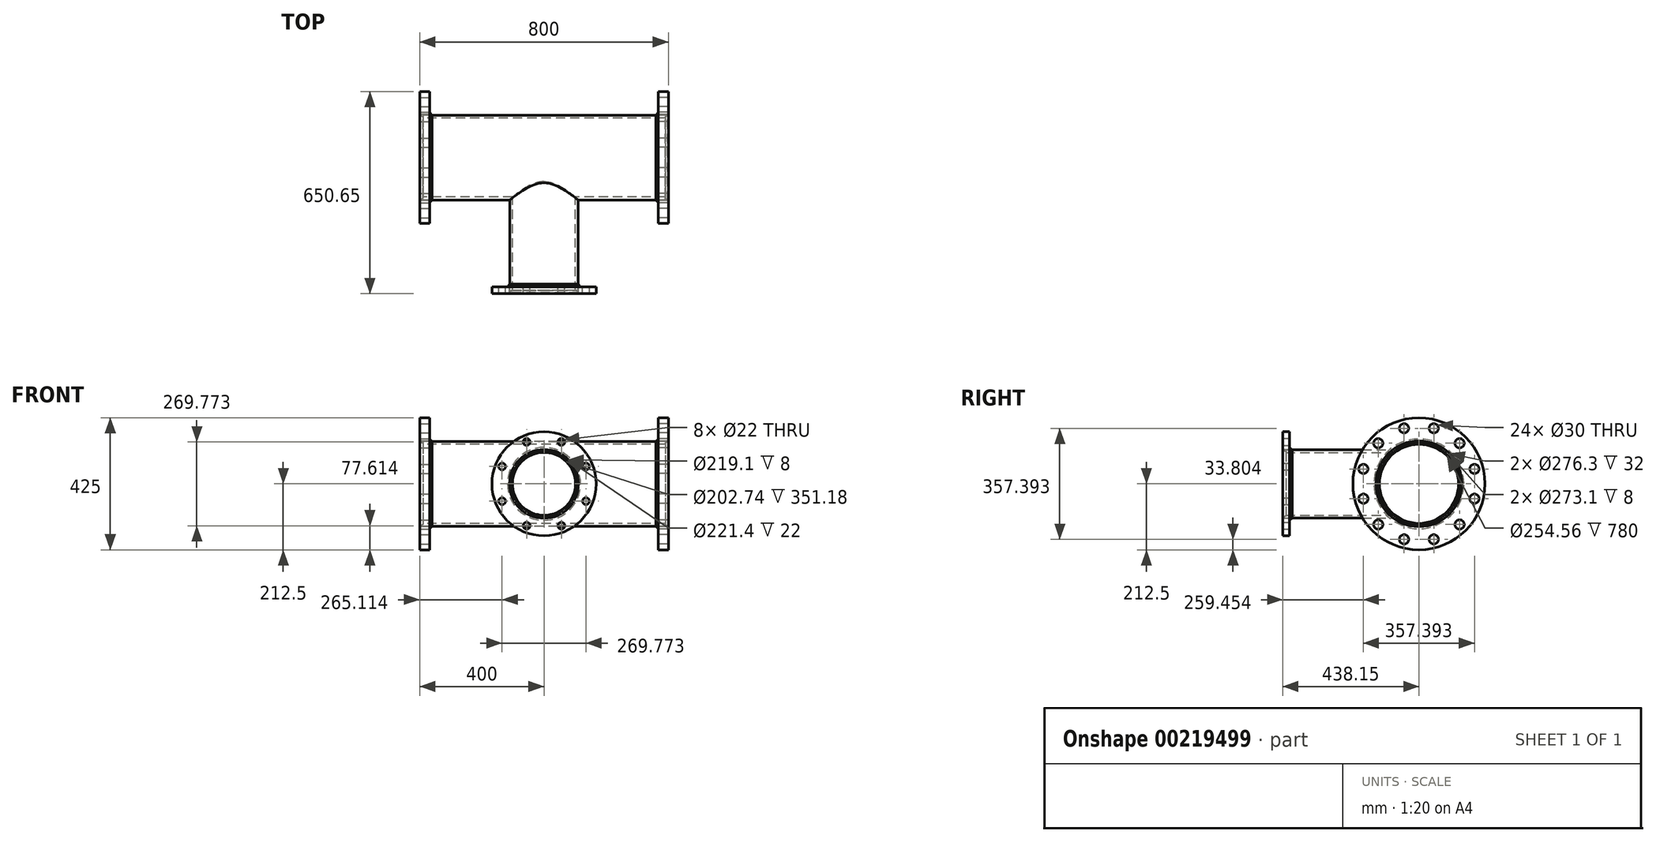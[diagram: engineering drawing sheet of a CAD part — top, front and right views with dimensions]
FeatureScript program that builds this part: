
annotation { "Feature Type Name" : "Feature", "Feature Type Description" : "" }
export const myFeature = defineFeature(function(context is Context, id is Id, definition is map)
    precondition{}
    {
        {
            var Q0;
            Q0=qCreatedBy(makeId("Front.planeOp"),FACE);
            var sketch = newSketch(context, id + "F0", { "sketchPlane" : qUnion([Q0])});
            skLineSegment(sketch, "E0", {"start": v(-484.3, 0) * mm, "end": v(476.6, 0) * mm, "construction": true});
            skLineSegment(sketch, "E1.bottom", {"start": v(-368, 138.15) * mm, "end": v(-400, 138.15) * mm});
            skLineSegment(sketch, "E1.top", {"start": v(-368, 212.5) * mm, "end": v(-400, 212.5) * mm});
            skLineSegment(sketch, "E1.left", {"start": v(-368, 138.15) * mm, "end": v(-368, 212.5) * mm});
            skLineSegment(sketch, "E1.right", {"start": v(-400, 138.15) * mm, "end": v(-400, 212.5) * mm});
            skLineSegment(sketch, "E2", {"start": v(0, 258.84) * mm, "end": v(0, -236.12) * mm, "construction": true});
            skLineSegment(sketch, "E3.bottom", {"start": v(0, 127.28) * mm, "end": v(-390, 127.28) * mm});
            skLineSegment(sketch, "E3.top", {"start": v(0, 136.55) * mm, "end": v(-390, 136.55) * mm});
            skLineSegment(sketch, "E3.left", {"start": v(0, 127.28) * mm, "end": v(0, 136.55) * mm});
            skLineSegment(sketch, "E3.right", {"start": v(-390, 127.28) * mm, "end": v(-390, 136.55) * mm});
            skLineSegment(sketch, "E4", {"start": v(-398, 138.15) * mm, "end": v(-390, 130.15) * mm});
            skLineSegment(sketch, "E5", {"start": v(-368, 138.15) * mm, "end": v(-368, 136.55) * mm});
            skLineSegment(sketch, "E6", {"start": v(-390, 138.15) * mm, "end": v(-390, 136.55) * mm});
            skLineSegment(sketch, "E7", {"start": v(-368, 144.55) * mm, "end": v(-360, 136.55) * mm});
            skLineSegment(sketch, "E8.MirrorCS", {"start": v(0, 136.55) * mm, "end": v(390, 136.55) * mm});
            skLineSegment(sketch, "E9.MirrorCS", {"start": v(0, 127.28) * mm, "end": v(390, 127.28) * mm});
            skLineSegment(sketch, "E10.MirrorCS", {"start": v(390, 127.28) * mm, "end": v(390, 136.55) * mm});
            skLineSegment(sketch, "E11.MirrorCS", {"start": v(398, 138.15) * mm, "end": v(390, 130.15) * mm});
            skLineSegment(sketch, "E12.MirrorCS", {"start": v(368, 144.55) * mm, "end": v(360, 136.55) * mm});
            skLineSegment(sketch, "E13.MirrorCS", {"start": v(368, 138.15) * mm, "end": v(400, 138.15) * mm});
            skLineSegment(sketch, "E14.MirrorCS", {"start": v(368, 138.15) * mm, "end": v(368, 136.55) * mm});
            skLineSegment(sketch, "E15.MirrorCS", {"start": v(368, 138.15) * mm, "end": v(368, 212.5) * mm});
            skLineSegment(sketch, "E16.MirrorCS", {"start": v(400, 138.15) * mm, "end": v(400, 212.5) * mm});
            skLineSegment(sketch, "E17.MirrorCS", {"start": v(368, 212.5) * mm, "end": v(400, 212.5) * mm});
            skLineSegment(sketch, "E18", {"start": v(390, 136.55) * mm, "end": v(390, 138.15) * mm});
            skSolve(sketch);
        }
        {
            var Q0;
            {var subQ0=sQuery(id+"F0.wireOp",EDGE,"E1.top");Q0=makeQuery(id+"F0.imprint","IMPRINT",FACE,{"disambiguationData":[TD([[makeQuery(id+"F0.imprint","IMPRINT",EDGE,{"derivedFrom":subQ0}),1.0]])]});}
            var Q1;
            Q1=sQuery(id+"F0.wireOp",EDGE,"E0");
            revolve(context, id + "F1", {"entities" : qUnion([Q0]), "axis" : qUnion([Q1]), "revolveType" : RevolveType.FULL});
        }
        {
            var Q0;
            {var subQ6=sQuery(id+"F0.wireOp",EDGE,"E16.MirrorCS");Q0=makeQuery(id+"F0.imprint","IMPRINT",FACE,{"disambiguationData":[TD([[makeQuery(id+"F0.imprint","IMPRINT",EDGE,{"derivedFrom":subQ6}),1.0]])]});}
            var Q1;
            Q1=sQuery(id+"F0.wireOp",EDGE,"E0");
            revolve(context, id + "F2", {"entities" : qUnion([Q0]), "axis" : qUnion([Q1]), "revolveType" : RevolveType.FULL});
        }
        {
            var Q0;
            {var subQ6=sQuery(id+"F0.wireOp",EDGE,"E3.bottom");Q0=makeQuery(id+"F0.imprint","IMPRINT",FACE,{"disambiguationData":[TD([[makeQuery(id+"F0.imprint","IMPRINT",EDGE,{"derivedFrom":subQ6}),-1.0]])]});}
            var Q1;
            {var subQ5=sQuery(id+"F0.wireOp",EDGE,"E3.left");Q1=makeQuery(id+"F0.imprint","IMPRINT",FACE,{"disambiguationData":[TD([[makeQuery(id+"F0.imprint","IMPRINT",EDGE,{"derivedFrom":subQ5}),-1.0]])]});}
            var Q2;
            Q2=sQuery(id+"F0.wireOp",EDGE,"E0");
            revolve(context, id + "F3", {"entities" : qUnion([Q0, Q1]), "axis" : qUnion([Q2]), "revolveType" : RevolveType.FULL});
        }
        {
            var Q0;
            {var subQ0=sQuery(id+"F0.wireOp",EDGE,"E4");Q0=makeQuery(id+"F0.imprint","IMPRINT",FACE,{"disambiguationData":[TD([[makeQuery(id+"F0.imprint","IMPRINT",EDGE,{"derivedFrom":subQ0}),1.0]])]});}
            var Q1;
            {var subQ0=sQuery(id+"F0.wireOp",EDGE,"E5");Q1=makeQuery(id+"F0.imprint","IMPRINT",FACE,{"disambiguationData":[TD([[makeQuery(id+"F0.imprint","IMPRINT",EDGE,{"derivedFrom":subQ0}),1.0]])]});}
            var Q2;
            {var subQ0=sQuery(id+"F0.wireOp",EDGE,"E12.MirrorCS");Q2=makeQuery(id+"F0.imprint","IMPRINT",FACE,{"disambiguationData":[TD([[makeQuery(id+"F0.imprint","IMPRINT",EDGE,{"derivedFrom":subQ0}),1.0]])]});}
            var Q3;
            {var subQ2=sQuery(id+"F0.wireOp",EDGE,"E11.MirrorCS");Q3=makeQuery(id+"F0.imprint","IMPRINT",FACE,{"disambiguationData":[TD([[makeQuery(id+"F0.imprint","IMPRINT",EDGE,{"derivedFrom":subQ2}),-1.0]])]});}
            var Q4;
            Q4=sQuery(id+"F0.wireOp",EDGE,"E0");
            revolve(context, id + "F4", {"entities" : qUnion([Q0, Q1, Q2, Q3]), "axis" : qUnion([Q4]), "revolveType" : RevolveType.FULL});
        }
        {
            var Q0;
            Q0=makeQuery(id+"F1.opRevolve","SWEPT_FACE",FACE,{"disambiguationData":[OSD([sQuery(id+"F0.wireOp",EDGE,"E1.right")])]});
            var sketch = newSketch(context, id + "F5", { "sketchPlane" : qUnion([Q0])});
            skCircle(sketch, "E19.cCircle", {"center": v(0, 0) * mm, "radius": 185 * mm, "construction": true});
            skLineSegment(sketch, "E19.0", {"start": v(-47.88, -178.7) * mm, "end": v(-130.81, -130.81) * mm});
            skLineSegment(sketch, "E19.1", {"start": v(-130.81, -130.81) * mm, "end": v(-178.7, -47.88) * mm});
            skLineSegment(sketch, "E19.2", {"start": v(-178.7, -47.88) * mm, "end": v(-178.7, 47.88) * mm});
            skLineSegment(sketch, "E19.3", {"start": v(-178.7, 47.88) * mm, "end": v(-130.81, 130.81) * mm});
            skLineSegment(sketch, "E19.4", {"start": v(-130.81, 130.81) * mm, "end": v(-47.88, 178.7) * mm});
            skLineSegment(sketch, "E19.5", {"start": v(-47.88, 178.7) * mm, "end": v(47.88, 178.7) * mm});
            skLineSegment(sketch, "E19.6", {"start": v(47.88, 178.7) * mm, "end": v(130.81, 130.81) * mm});
            skLineSegment(sketch, "E19.7", {"start": v(130.81, 130.81) * mm, "end": v(178.7, 47.88) * mm});
            skLineSegment(sketch, "E19.8", {"start": v(178.7, 47.88) * mm, "end": v(178.7, -47.88) * mm});
            skLineSegment(sketch, "E19.9", {"start": v(178.7, -47.88) * mm, "end": v(130.81, -130.81) * mm});
            skLineSegment(sketch, "E19.10", {"start": v(130.81, -130.81) * mm, "end": v(47.88, -178.7) * mm});
            skLineSegment(sketch, "E19.11", {"start": v(47.88, -178.7) * mm, "end": v(-47.88, -178.7) * mm});
            skPoint(sketch, "E20", {"position": v(178.7, 47.88) * mm});
            skPoint(sketch, "E21", {"position": v(178.7, -47.88) * mm});
            skPoint(sketch, "E22", {"position": v(130.81, -130.81) * mm});
            skPoint(sketch, "E23", {"position": v(47.88, -178.7) * mm});
            skPoint(sketch, "E24", {"position": v(-47.88, -178.7) * mm});
            skPoint(sketch, "E25", {"position": v(-130.81, -130.81) * mm});
            skPoint(sketch, "E26", {"position": v(-178.7, -47.88) * mm});
            skPoint(sketch, "E27", {"position": v(-178.7, 47.88) * mm});
            skPoint(sketch, "E28", {"position": v(-130.81, 130.81) * mm});
            skPoint(sketch, "E29", {"position": v(-47.88, 178.7) * mm});
            skPoint(sketch, "E30", {"position": v(47.88, 178.7) * mm});
            skPoint(sketch, "E31", {"position": v(130.81, 130.81) * mm});
            skSolve(sketch);
        }
        {
            var Q0;
            Q0=sQuery(id+"F5.wireOp",VERTEX,"E20");
            var Q1;
            Q1=sQuery(id+"F5.wireOp",VERTEX,"E21");
            var Q2;
            Q2=sQuery(id+"F5.wireOp",VERTEX,"E22");
            var Q3;
            Q3=sQuery(id+"F5.wireOp",VERTEX,"E23");
            var Q4;
            Q4=sQuery(id+"F5.wireOp",VERTEX,"E24");
            var Q5;
            Q5=sQuery(id+"F5.wireOp",VERTEX,"E25");
            var Q6;
            Q6=sQuery(id+"F5.wireOp",VERTEX,"E26");
            var Q7;
            Q7=sQuery(id+"F5.wireOp",VERTEX,"E27");
            var Q8;
            Q8=sQuery(id+"F5.wireOp",VERTEX,"E28");
            var Q9;
            Q9=sQuery(id+"F5.wireOp",VERTEX,"E29");
            var Q10;
            Q10=sQuery(id+"F5.wireOp",VERTEX,"E30");
            var Q11;
            Q11=sQuery(id+"F5.wireOp",VERTEX,"E31");
            var Q12;
            Q12=makeQuery(id+"F1.opRevolve","SWEPT_BODY",BODY,{"disambiguationData":[OSD([sQuery(id+"F0.wireOp",EDGE,"E1.bottom"),sQuery(id+"F0.wireOp",EDGE,"E1.top"),sQuery(id+"F0.wireOp",EDGE,"E1.left"),sQuery(id+"F0.wireOp",EDGE,"E1.right")])]});
            hole(context, id + "F6", {"style" : HoleStyle.SIMPLE, "endStyle" : HoleEndStyle.BLIND, "holeDiameter" : 30 * mm, "holeDepth" : 50 * mm, "locations" : qUnion([Q0, Q1, Q2, Q3, Q4, Q5, Q6, Q7, Q8, Q9, Q10, Q11]), "scope" : qUnion([Q12])});
        }
        {
            var Q0;
            Q0=makeQuery(id+"F2.opRevolve","SWEPT_FACE",FACE,{"disambiguationData":[OSD([sQuery(id+"F0.wireOp",EDGE,"E16.MirrorCS")])]});
            var sketch = newSketch(context, id + "F7", { "sketchPlane" : qUnion([Q0])});
            skCircle(sketch, "E32.cCircle", {"center": v(0, 0) * mm, "radius": 185 * mm, "construction": true});
            skLineSegment(sketch, "E32.0", {"start": v(-130.81, -130.81) * mm, "end": v(-178.7, -47.88) * mm});
            skLineSegment(sketch, "E32.1", {"start": v(-178.7, -47.88) * mm, "end": v(-178.7, 47.88) * mm});
            skLineSegment(sketch, "E32.2", {"start": v(-178.7, 47.88) * mm, "end": v(-130.81, 130.81) * mm});
            skLineSegment(sketch, "E32.3", {"start": v(-130.81, 130.81) * mm, "end": v(-47.88, 178.7) * mm});
            skLineSegment(sketch, "E32.4", {"start": v(-47.88, 178.7) * mm, "end": v(47.88, 178.7) * mm});
            skLineSegment(sketch, "E32.5", {"start": v(47.88, 178.7) * mm, "end": v(130.81, 130.81) * mm});
            skLineSegment(sketch, "E32.6", {"start": v(130.81, 130.81) * mm, "end": v(178.7, 47.88) * mm});
            skLineSegment(sketch, "E32.7", {"start": v(178.7, 47.88) * mm, "end": v(178.7, -47.88) * mm});
            skLineSegment(sketch, "E32.8", {"start": v(178.7, -47.88) * mm, "end": v(130.81, -130.81) * mm});
            skLineSegment(sketch, "E32.9", {"start": v(130.81, -130.81) * mm, "end": v(47.88, -178.7) * mm});
            skLineSegment(sketch, "E32.10", {"start": v(47.88, -178.7) * mm, "end": v(-47.88, -178.7) * mm});
            skLineSegment(sketch, "E32.11", {"start": v(-47.88, -178.7) * mm, "end": v(-130.81, -130.81) * mm});
            skPoint(sketch, "E33", {"position": v(-178.7, -47.88) * mm});
            skPoint(sketch, "E34", {"position": v(-178.7, 47.88) * mm});
            skPoint(sketch, "E35", {"position": v(-130.81, 130.81) * mm});
            skPoint(sketch, "E36", {"position": v(-47.88, 178.7) * mm});
            skPoint(sketch, "E37", {"position": v(47.88, 178.7) * mm});
            skPoint(sketch, "E38", {"position": v(130.81, 130.81) * mm});
            skPoint(sketch, "E39", {"position": v(178.7, 47.88) * mm});
            skPoint(sketch, "E40", {"position": v(178.7, -47.88) * mm});
            skPoint(sketch, "E41", {"position": v(47.88, -178.7) * mm});
            skPoint(sketch, "E42", {"position": v(-47.88, -178.7) * mm});
            skPoint(sketch, "E43", {"position": v(-130.81, -130.81) * mm});
            skSolve(sketch);
        }
        {
            var Q0;
            Q0=sQuery(id+"F7.wireOp",VERTEX,"E43");
            var Q1;
            Q1=sQuery(id+"F7.wireOp",VERTEX,"E33");
            var Q2;
            Q2=sQuery(id+"F7.wireOp",VERTEX,"E34");
            var Q3;
            Q3=sQuery(id+"F7.wireOp",VERTEX,"E35");
            var Q4;
            Q4=sQuery(id+"F7.wireOp",VERTEX,"E36");
            var Q5;
            Q5=sQuery(id+"F7.wireOp",VERTEX,"E37");
            var Q6;
            Q6=sQuery(id+"F7.wireOp",VERTEX,"E38");
            var Q7;
            Q7=sQuery(id+"F7.wireOp",VERTEX,"E39");
            var Q8;
            Q8=sQuery(id+"F7.wireOp",VERTEX,"E40");
            var Q9;
            Q9=sQuery(id+"F7.wireOp",VERTEX,"E32.9.start");
            var Q10;
            Q10=sQuery(id+"F7.wireOp",VERTEX,"E41");
            var Q11;
            Q11=sQuery(id+"F7.wireOp",VERTEX,"E42");
            var Q12;
            Q12=makeQuery(id+"F2.opRevolve","SWEPT_BODY",BODY,{"disambiguationData":[OSD([sQuery(id+"F0.wireOp",EDGE,"E13.MirrorCS"),sQuery(id+"F0.wireOp",EDGE,"E15.MirrorCS"),sQuery(id+"F0.wireOp",EDGE,"E16.MirrorCS"),sQuery(id+"F0.wireOp",EDGE,"E17.MirrorCS")])]});
            hole(context, id + "F8", {"style" : HoleStyle.SIMPLE, "endStyle" : HoleEndStyle.BLIND, "holeDiameter" : 30 * mm, "holeDepth" : 50 * mm, "locations" : qUnion([Q0, Q1, Q2, Q3, Q4, Q5, Q6, Q7, Q8, Q9, Q10, Q11]), "scope" : qUnion([Q12])});
        }
        {
            var Q0;
            Q0=qCreatedBy(makeId("Right.planeOp"),FACE);
            var sketch = newSketch(context, id + "F9", { "sketchPlane" : qUnion([Q0])});
            skLineSegment(sketch, "E44", {"start": v(0, 0) * mm, "end": v(-731.65, 0) * mm, "construction": true});
            skLineSegment(sketch, "E45.bottom", {"start": v(0, -101.37) * mm, "end": v(-428.15, -101.37) * mm});
            skLineSegment(sketch, "E45.top", {"start": v(0, -109.55) * mm, "end": v(-428.15, -109.55) * mm});
            skLineSegment(sketch, "E45.left", {"start": v(0, -101.37) * mm, "end": v(0, -109.55) * mm});
            skLineSegment(sketch, "E45.right", {"start": v(-428.15, -101.37) * mm, "end": v(-428.15, -109.55) * mm});
            skLineSegment(sketch, "E46.bottom", {"start": v(-416.15, -110.7) * mm, "end": v(-438.15, -110.7) * mm});
            skLineSegment(sketch, "E46.top", {"start": v(-416.15, -167.5) * mm, "end": v(-438.15, -167.5) * mm});
            skLineSegment(sketch, "E46.left", {"start": v(-416.15, -110.7) * mm, "end": v(-416.15, -167.5) * mm});
            skLineSegment(sketch, "E46.right", {"start": v(-438.15, -110.7) * mm, "end": v(-438.15, -167.5) * mm});
            skLineSegment(sketch, "E47", {"start": v(-416.15, -110.7) * mm, "end": v(-416.15, -109.55) * mm});
            skLineSegment(sketch, "E48", {"start": v(-416.15, -117.55) * mm, "end": v(-408.15, -109.55) * mm});
            skLineSegment(sketch, "E49", {"start": v(-428.15, -110.7) * mm, "end": v(-428.15, -109.55) * mm});
            skLineSegment(sketch, "E50", {"start": v(-436.15, -110.7) * mm, "end": v(-428.15, -102.7) * mm});
            skSolve(sketch);
        }
        {
            var Q0;
            {var subQ6=sQuery(id+"F9.wireOp",EDGE,"E45.bottom");Q0=makeQuery(id+"F9.imprint","IMPRINT",FACE,{"disambiguationData":[TD([[makeQuery(id+"F9.imprint","IMPRINT",EDGE,{"derivedFrom":subQ6}),1.0]])]});}
            var Q1;
            Q1=sQuery(id+"F9.wireOp",EDGE,"E44");
            revolve(context, id + "F10", {"operationType" : NewBodyOperationType.ADD, "entities" : qUnion([Q0]), "axis" : qUnion([Q1]), "revolveType" : RevolveType.FULL});
        }
        {
            var Q0;
            {var subQ3=sQuery(id+"F9.wireOp",EDGE,"E46.top");Q0=makeQuery(id+"F9.imprint","IMPRINT",FACE,{"disambiguationData":[TD([[makeQuery(id+"F9.imprint","IMPRINT",EDGE,{"derivedFrom":subQ3}),-1.0]])]});}
            var Q1;
            Q1=sQuery(id+"F9.wireOp",EDGE,"E44");
            revolve(context, id + "F11", {"entities" : qUnion([Q0]), "axis" : qUnion([Q1]), "revolveType" : RevolveType.FULL});
        }
        {
            var Q0;
            {var subQ0=sQuery(id+"F9.wireOp",EDGE,"E47");Q0=makeQuery(id+"F9.imprint","IMPRINT",FACE,{"disambiguationData":[TD([[makeQuery(id+"F9.imprint","IMPRINT",EDGE,{"derivedFrom":subQ0}),-1.0]])]});}
            var Q1;
            {var subQ0=sQuery(id+"F9.wireOp",EDGE,"E49");Q1=makeQuery(id+"F9.imprint","IMPRINT",FACE,{"disambiguationData":[TD([[makeQuery(id+"F9.imprint","IMPRINT",EDGE,{"derivedFrom":subQ0}),1.0]])]});}
            var Q2;
            Q2=sQuery(id+"F9.wireOp",EDGE,"E44");
            revolve(context, id + "F12", {"entities" : qUnion([Q0, Q1]), "axis" : qUnion([Q2]), "revolveType" : RevolveType.FULL});
        }
        {
            var Q0;
            Q0=makeQuery(id+"F11.opRevolve","SWEPT_FACE",FACE,{"disambiguationData":[OSD([sQuery(id+"F9.wireOp",EDGE,"E46.right")])]});
            var sketch = newSketch(context, id + "F13", { "sketchPlane" : qUnion([Q0])});
            skCircle(sketch, "E51.cCircle", {"center": v(0, 0) * mm, "radius": 146 * mm, "construction": true});
            skLineSegment(sketch, "E51.0", {"start": v(55.87, 134.89) * mm, "end": v(134.89, 55.87) * mm});
            skLineSegment(sketch, "E51.1", {"start": v(134.89, 55.87) * mm, "end": v(134.89, -55.87) * mm});
            skLineSegment(sketch, "E51.2", {"start": v(134.89, -55.87) * mm, "end": v(55.87, -134.89) * mm});
            skLineSegment(sketch, "E51.3", {"start": v(55.87, -134.89) * mm, "end": v(-55.87, -134.89) * mm});
            skLineSegment(sketch, "E51.4", {"start": v(-55.87, -134.89) * mm, "end": v(-134.89, -55.87) * mm});
            skLineSegment(sketch, "E51.5", {"start": v(-134.89, -55.87) * mm, "end": v(-134.89, 55.87) * mm});
            skLineSegment(sketch, "E51.6", {"start": v(-134.89, 55.87) * mm, "end": v(-55.87, 134.89) * mm});
            skLineSegment(sketch, "E51.7", {"start": v(-55.87, 134.89) * mm, "end": v(55.87, 134.89) * mm});
            skPoint(sketch, "E52", {"position": v(-55.87, 134.89) * mm});
            skPoint(sketch, "E53", {"position": v(55.87, 134.89) * mm});
            skPoint(sketch, "E54", {"position": v(134.89, 55.87) * mm});
            skPoint(sketch, "E55", {"position": v(134.89, -55.87) * mm});
            skPoint(sketch, "E56", {"position": v(55.87, -134.89) * mm});
            skPoint(sketch, "E57", {"position": v(-55.87, -134.89) * mm});
            skPoint(sketch, "E58", {"position": v(-134.89, -55.87) * mm});
            skPoint(sketch, "E59", {"position": v(-134.89, 55.87) * mm});
            skSolve(sketch);
        }
        {
            var Q0;
            Q0=sQuery(id+"F13.wireOp",VERTEX,"E51.6.end");
            var Q1;
            Q1=sQuery(id+"F13.wireOp",VERTEX,"E53");
            var Q2;
            Q2=sQuery(id+"F13.wireOp",VERTEX,"E51.0.end");
            var Q3;
            Q3=sQuery(id+"F13.wireOp",VERTEX,"E51.2.start");
            var Q4;
            Q4=sQuery(id+"F13.wireOp",VERTEX,"E56");
            var Q5;
            Q5=sQuery(id+"F13.wireOp",VERTEX,"E51.4.start");
            var Q6;
            Q6=sQuery(id+"F13.wireOp",VERTEX,"E58");
            var Q7;
            Q7=sQuery(id+"F13.wireOp",VERTEX,"E51.6.start");
            var Q8;
            Q8=makeQuery(id+"F11.opRevolve","SWEPT_BODY",BODY,{"disambiguationData":[OSD([sQuery(id+"F9.wireOp",EDGE,"E46.bottom"),sQuery(id+"F9.wireOp",EDGE,"E46.top"),sQuery(id+"F9.wireOp",EDGE,"E46.left"),sQuery(id+"F9.wireOp",EDGE,"E46.right")])]});
            hole(context, id + "F14", {"style" : HoleStyle.SIMPLE, "endStyle" : HoleEndStyle.BLIND, "holeDiameter" : 22 * mm, "holeDepth" : 50 * mm, "locations" : qUnion([Q0, Q1, Q2, Q3, Q4, Q5, Q6, Q7]), "scope" : qUnion([Q8])});
        }
        {
            var Q0;
            Q0=makeQuery(id+"F1.opRevolve","SWEPT_FACE",FACE,{"disambiguationData":[OSD([sQuery(id+"F0.wireOp",EDGE,"E1.right")])]});
            var sketch = newSketch(context, id + "F15", { "sketchPlane" : qUnion([Q0])});
            skCircle(sketch, "E60", {"center": v(0, 0) * mm, "radius": 127.28 * mm});
            skSolve(sketch);
        }
        {
            var Q0;
            Q0=makeQuery(id+"F15.imprint","IMPRINT",FACE,{"disambiguationData":[TD([[makeQuery(id+"F15.imprint","IMPRINT",EDGE,{"derivedFrom":sQuery(id+"F15.wireOp",EDGE,"E60")}),1.0]])]});
            extrude(context, id + "F16", {"entities" : qUnion([Q0]), "operationType" : NewBodyOperationType.REMOVE, "endBound" : BoundingType.THROUGH_ALL, "oppositeDirection" : true, "depth" : 25 * mm});
        }
        {
            var Q0;
            Q0=makeQuery(id+"F11.opRevolve","SWEPT_FACE",FACE,{"disambiguationData":[OSD([sQuery(id+"F9.wireOp",EDGE,"E46.right")])]});
            var sketch = newSketch(context, id + "F17", { "sketchPlane" : qUnion([Q0])});
            skCircle(sketch, "E61", {"center": v(0, 0) * mm, "radius": 101.37 * mm});
            skSolve(sketch);
        }
        {
            var Q0;
            Q0=makeQuery(id+"F17.imprint","IMPRINT",FACE,{"disambiguationData":[TD([[makeQuery(id+"F17.imprint","IMPRINT",EDGE,{"derivedFrom":sQuery(id+"F17.wireOp",EDGE,"E61")}),1.0]])]});
            extrude(context, id + "F18", {"entities" : qUnion([Q0]), "operationType" : NewBodyOperationType.REMOVE, "oppositeDirection" : true, "depth" : 393 * mm});
        }
    });
